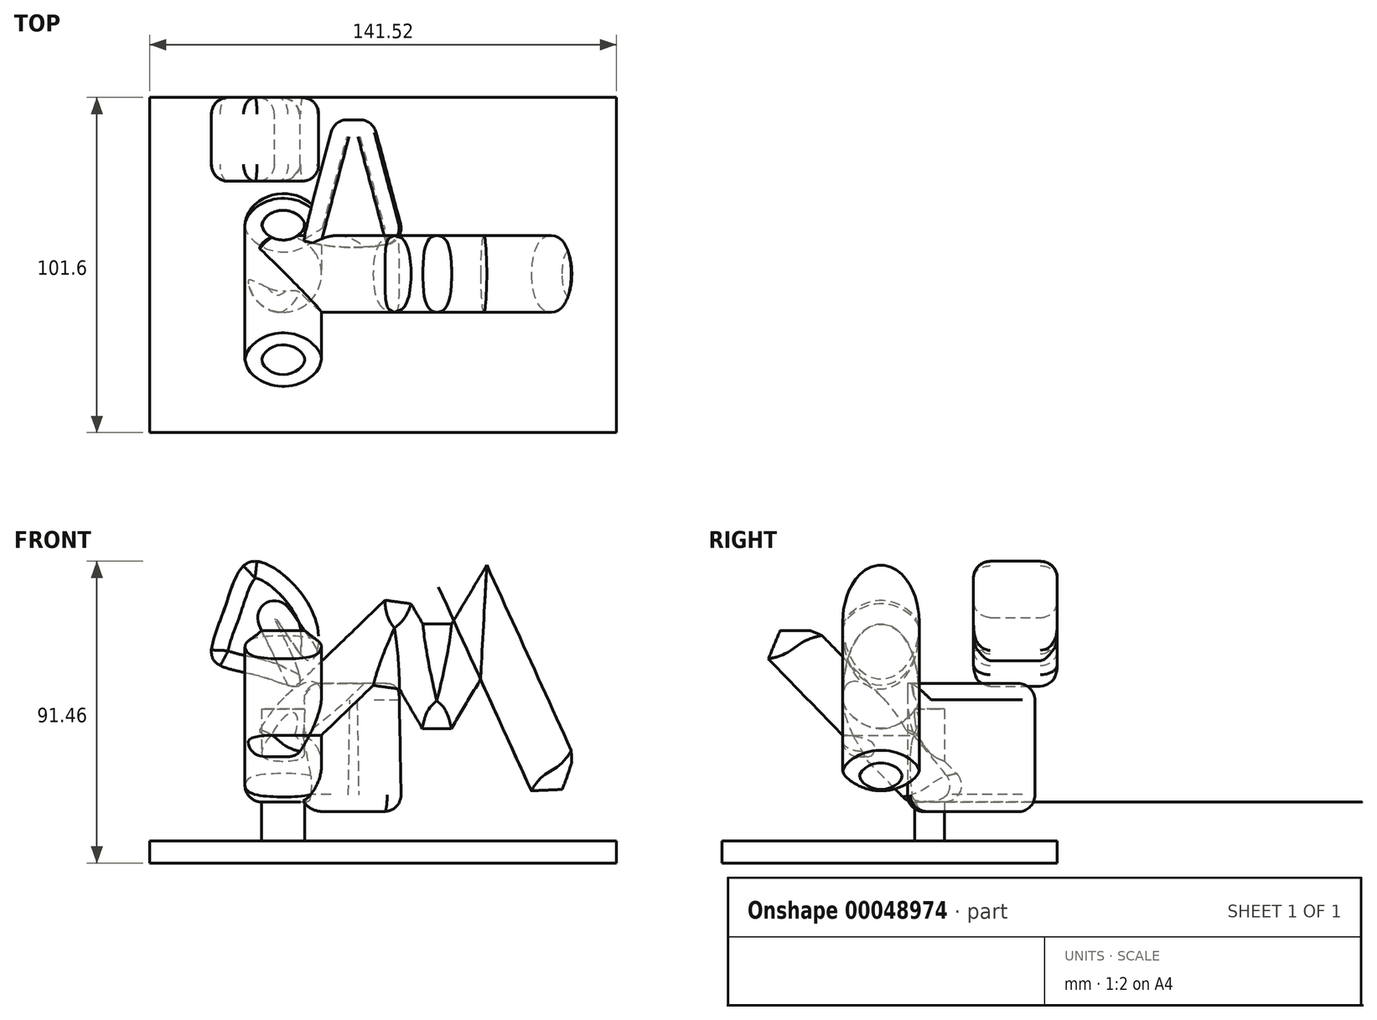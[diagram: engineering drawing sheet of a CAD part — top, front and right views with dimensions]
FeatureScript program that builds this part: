
annotation { "Feature Type Name" : "Feature", "Feature Type Description" : "" }
export const myFeature = defineFeature(function(context is Context, id is Id, definition is map)
    precondition{}
    {
        {
            var Q0;
            Q0=qCreatedBy(makeId("Front.planeOp"),FACE);
            var sketch = newSketch(context, id + "F0", { "sketchPlane" : qUnion([Q0])});
            skFitSpline(sketch, "E0", {"points": [v(-11.66, 35.52) * mm, v(-30.7, 52.67) * mm, v(-39.27, 37.93) * mm, v(-42.48, 22.92) * mm, v(-27.2, 17.56) * mm, v(-16.22, 15.95) * mm, v(-23.99, 35.52) * mm, v(-19.97, 30.15) * mm, v(-13, 22.65) * mm, v(-11.66, 35.52) * mm]});
            skSolve(sketch);
        }
        {
            var Q0;
            Q0=makeQuery(id+"F0.imprint","IMPRINT",FACE,{"disambiguationData":[TD([[makeQuery(id+"F0.imprint","IMPRINT",EDGE,{"derivedFrom":sQuery(id+"F0.wireOp",EDGE,"E0")}),1.0]])]});
            extrude(context, id + "F1", {"entities" : qUnion([Q0]), "depth" : 25.4 * mm});
        }
        {
            var Q0;
            Q0=qCreatedBy(makeId("Right.planeOp"),FACE);
            var sketch = newSketch(context, id + "F2", { "sketchPlane" : qUnion([Q0])});
            skLineSegment(sketch, "E1.bottom", {"start": v(-45.43, 15.68) * mm, "end": v(-6.84, 15.68) * mm});
            skLineSegment(sketch, "E1.top", {"start": v(-45.43, -23.19) * mm, "end": v(-6.84, -23.19) * mm});
            skLineSegment(sketch, "E1.left", {"start": v(-45.43, 15.68) * mm, "end": v(-45.43, -23.19) * mm});
            skLineSegment(sketch, "E1.right", {"start": v(-6.84, 15.68) * mm, "end": v(-6.84, -23.19) * mm});
            skLineSegment(sketch, "E2", {"start": v(-53.47, -19.97) * mm, "end": v(-12.2, 31.76) * mm});
            skLineSegment(sketch, "E3", {"start": v(-12.2, 31.76) * mm, "end": v(38.46, -20.24) * mm});
            skLineSegment(sketch, "E4", {"start": v(16.75, -41.5) * mm, "end": v(10.86, 39.23) * mm});
            skSolve(sketch);
        }
        {
            var Q0;
            Q0=qCreatedBy(makeId("Top.planeOp"),FACE);
            var sketch = newSketch(context, id + "F3", { "sketchPlane" : qUnion([Q0])});
            skCircle(sketch, "E5", {"center": v(-21.3, -53.47) * mm, "radius": 11.6 * mm});
            skSolve(sketch);
        }
        {
            var Q0;
            Q0 = qSketchRegion(id + "F2", true);
            var Q1;
            Q1=sQuery(id+"F2.wireOp",EDGE,"E4");
            revolve(context, id + "F4", {"entities" : qUnion([Q0]), "axis" : qUnion([Q1]), "revolveType" : RevolveType.SYMMETRIC, "angle" : 30 * degree});
        }
        {
            var Q0;
            Q0=qCreatedBy(makeId("Front.planeOp"),FACE);
            var sketch = newSketch(context, id + "F5", { "sketchPlane" : qUnion([Q0])});
            skLineSegment(sketch, "E6", {"start": v(-39, -6.57) * mm, "end": v(14.07, 44.63) * mm});
            skLineSegment(sketch, "E7", {"start": v(14.07, 44.63) * mm, "end": v(25.33, 25.33) * mm});
            skLineSegment(sketch, "E8", {"start": v(25.33, 25.33) * mm, "end": v(40.34, 50.53) * mm});
            skLineSegment(sketch, "E9", {"start": v(40.34, 50.53) * mm, "end": v(66.6, -7.1) * mm});
            skSolve(sketch);
        }
        {
            var Q0;
            Q0=makeQuery(id+"F3.imprint","IMPRINT",FACE,{"disambiguationData":[TD([[makeQuery(id+"F3.imprint","IMPRINT",EDGE,{"derivedFrom":sQuery(id+"F3.wireOp",EDGE,"E5")}),1.0]])]});
            var Q1;
            Q1=sQuery(id+"F5.wireOp",EDGE,"E6");
            var Q2;
            Q2=sQuery(id+"F5.wireOp",EDGE,"E7");
            var Q3;
            Q3=sQuery(id+"F5.wireOp",EDGE,"E8");
            var Q4;
            Q4=sQuery(id+"F5.wireOp",EDGE,"E9");
            sweep(context, id + "F6", {"operationType" : NewBodyOperationType.ADD, "profiles" : qUnion([Q0]), "path" : qUnion([Q1, Q2, Q3, Q4])});
        }
        {
            var Q0;
            Q0 = qSketchRegion(id + "F3", true);
            var Q1;
            Q1=sQuery(id+"F2.wireOp",EDGE,"E3");
            sweep(context, id + "F7", {"profiles" : qUnion([Q0]), "path" : qUnion([Q1])});
        }
        {
            var Q0;
            Q0=makeQuery(id+"F6.opSweep","CAP_EDGE",EDGE,{"disambiguationData":[OSD([sQuery(id+"F3.wireOp",EDGE,"E5"),sQuery(id+"F5.wireOp",VERTEX,"E6.start")])],"isStart":true});
            fillet(context, id + "F8", {"entities" : qUnion([Q0]), "radius" : 5.08 * mm, "tangentPropagation" : true, "allowEdgeOverflow" : false});
        }
        {
            var Q0;
            Q0=makeQuery(id+"F7.opSweep","CAP_EDGE",EDGE,{"disambiguationData":[OSD([sQuery(id+"F2.wireOp",VERTEX,"E3.end"),sQuery(id+"F3.wireOp",EDGE,"E5")])],"isStart":true});
            fillet(context, id + "F9", {"entities" : qUnion([Q0]), "radius" : 5.08 * mm, "tangentPropagation" : true, "allowEdgeOverflow" : false});
        }
        {
            var Q0;
            Q0=makeQuery(id+"F4.opRevolve","CAP_EDGE",EDGE,{"disambiguationData":[OSD([sQuery(id+"F2.wireOp",EDGE,"E1.left")])],"isStart":false});
            var Q1;
            Q1=makeQuery(id+"F4.opRevolve","SWEPT_EDGE",EDGE,{"disambiguationData":[OSD([sQuery(id+"F2.wireOp",EDGE,"E1.top"),sQuery(id+"F2.wireOp",EDGE,"E1.left")])]});
            var Q2;
            Q2=makeQuery(id+"F4.opRevolve","CAP_EDGE",EDGE,{"disambiguationData":[OSD([sQuery(id+"F2.wireOp",EDGE,"E1.top")])],"isStart":true});
            var Q3;
            Q3=makeQuery(id+"F4.opRevolve","CAP_EDGE",EDGE,{"disambiguationData":[OSD([sQuery(id+"F2.wireOp",EDGE,"E1.top")])],"isStart":false});
            var Q4;
            Q4=makeQuery(id+"F4.opRevolve","SWEPT_EDGE",EDGE,{"disambiguationData":[OSD([sQuery(id+"F2.wireOp",EDGE,"E1.top"),sQuery(id+"F2.wireOp",EDGE,"E1.right")])]});
            var Q5;
            Q5=makeQuery(id+"F4.opRevolve","CAP_EDGE",EDGE,{"disambiguationData":[OSD([sQuery(id+"F2.wireOp",EDGE,"E1.right")])],"isStart":false});
            var Q6;
            Q6=makeQuery(id+"F4.opRevolve","CAP_EDGE",EDGE,{"disambiguationData":[OSD([sQuery(id+"F2.wireOp",EDGE,"E1.right")])],"isStart":true});
            var Q7;
            Q7=makeQuery(id+"F4.opRevolve","CAP_EDGE",EDGE,{"disambiguationData":[OSD([sQuery(id+"F2.wireOp",EDGE,"E1.bottom")])],"isStart":false});
            var Q8;
            Q8=makeQuery(id+"F4.opRevolve","CAP_EDGE",EDGE,{"disambiguationData":[OSD([sQuery(id+"F2.wireOp",EDGE,"E1.bottom")])],"isStart":true});
            var Q9;
            Q9=makeQuery(id+"F4.opRevolve","SWEPT_EDGE",EDGE,{"disambiguationData":[OSD([sQuery(id+"F2.wireOp",EDGE,"E1.bottom"),sQuery(id+"F2.wireOp",EDGE,"E1.right")])]});
            fillet(context, id + "F10", {"entities" : qUnion([Q0, Q1, Q2, Q3, Q4, Q5, Q6, Q7, Q8, Q9]), "radius" : 5.08 * mm, "tangentPropagation" : true, "allowEdgeOverflow" : false});
        }
        {
            var Q0;
            Q0=makeQuery(id+"F6.opSweep","MID_CAP_EDGE",EDGE,{"disambiguationData":[OSD([sQuery(id+"F3.wireOp",EDGE,"E5"),sQuery(id+"F5.wireOp",VERTEX,"E8.start")])],"capPos":2.0});
            var Q1;
            Q1=makeQuery(id+"F6.opSweep","CAP_EDGE",EDGE,{"disambiguationData":[OSD([sQuery(id+"F3.wireOp",EDGE,"E5"),sQuery(id+"F5.wireOp",VERTEX,"E9.end")])],"isStart":false});
            var Q2;
            Q2=makeQuery(id+"F6.opSweep","MID_CAP_EDGE",EDGE,{"disambiguationData":[OSD([sQuery(id+"F3.wireOp",EDGE,"E5"),sQuery(id+"F5.wireOp",VERTEX,"E7.start")])],"capPos":1.0});
            var Q3;
            Q3=makeQuery(id+"F7.opSweep","CAP_EDGE",EDGE,{"disambiguationData":[OSD([sQuery(id+"F2.wireOp",VERTEX,"E3.start"),sQuery(id+"F3.wireOp",EDGE,"E5")])],"isStart":false});
            chamfer(context, id + "F11", {"entities" : qUnion([Q0, Q1, Q2, Q3]), "width" : 5.08 * mm, "tangentPropagation" : true});
        }
        {
            var Q0;
            Q0=makeQuery(id+"F1.opExtrude","CAP_EDGE",EDGE,{"disambiguationData":[OSD([sQuery(id+"F0.wireOp",EDGE,"E0")])],"isStart":false});
            var Q1;
            Q1=makeQuery(id+"F1.opExtrude","CAP_EDGE",EDGE,{"disambiguationData":[OSD([sQuery(id+"F0.wireOp",EDGE,"E0")])],"isStart":true});
            fillet(context, id + "F12", {"entities" : qUnion([Q0, Q1]), "radius" : 5.08 * mm, "tangentPropagation" : true, "allowEdgeOverflow" : false});
        }
        {
            var Q0;
            Q0=qCreatedBy(makeId("Front.planeOp"),FACE);
            var sketch = newSketch(context, id + "F13", { "sketchPlane" : qUnion([Q0])});
            skLineSegment(sketch, "E10.bottom", {"start": v(-61.78, -32.03) * mm, "end": v(79.74, -32.03) * mm});
            skLineSegment(sketch, "E10.top", {"start": v(-61.78, -38.73) * mm, "end": v(79.74, -38.73) * mm});
            skLineSegment(sketch, "E10.left", {"start": v(-61.78, -32.03) * mm, "end": v(-61.78, -38.73) * mm});
            skLineSegment(sketch, "E10.right", {"start": v(79.74, -32.03) * mm, "end": v(79.74, -38.73) * mm});
            skLineSegment(sketch, "E11", {"start": v(-21.68, 7.9) * mm, "end": v(-21.68, -32.03) * mm});
            skLineSegment(sketch, "E12", {"start": v(0, -23.19) * mm, "end": v(0, -32.03) * mm});
            skLineSegment(sketch, "E13", {"start": v(50.96, -32.03) * mm, "end": v(50.96, -8.44) * mm});
            skSolve(sketch);
        }
        {
            var Q0;
            Q0=makeQuery(id+"F13.imprint","IMPRINT",FACE,{"disambiguationData":[TD([[makeQuery(id+"F13.imprint","IMPRINT",EDGE,{"derivedFrom":sQuery(id+"F13.wireOp",EDGE,"E10.bottom")}),-1.0]])]});
            extrude(context, id + "F14", {"entities" : qUnion([Q0]), "depth" : 101.6 * mm});
        }
        {
            var Q0;
            Q0 = qSketchRegion(id + "F13", true);
            extrude(context, id + "F15", {"entities" : qUnion([Q0]), "operationType" : NewBodyOperationType.ADD, "depth" : 25.4 * mm});
        }
        {
            var Q0;
            Q0=makeQuery(id+"F7.opSweep","CAP_FACE",FACE,{"disambiguationData":[OSD([sQuery(id+"F2.wireOp",VERTEX,"E3.end"),sQuery(id+"F3.wireOp",EDGE,"E5")])],"isStart":true});
            var Q1;
            {var subQ0=sQuery(id+"F3.wireOp",EDGE,"E5");var subQ1=sQuery(id+"F2.wireOp",VERTEX,"E3.end");Q1=makeQuery(id+"F9.opFillet","BLEND_EDGE",EDGE,{"blendedFrom":[makeQuery(id+"F7.opSweep","CAP_EDGE",EDGE,{"disambiguationData":[OSD([subQ1,subQ0])],"isStart":true}),makeQuery(id+"F7.opSweep","CAP_FACE",FACE,{"disambiguationData":[OSD([subQ1,subQ0])],"isStart":true})],"blendedInto":[makeQuery(id+"F7.opSweep","CAP_FACE",FACE,{"disambiguationData":[OSD([subQ1,subQ0])],"isStart":true})]});}
            var Q2;
            Q2=sQuery(id+"F13.wireOp",EDGE,"E11");
            sweep(context, id + "F16", {"operationType" : NewBodyOperationType.ADD, "profiles" : qUnion([Q0]), "surfaceProfiles" : qUnion([Q1]), "path" : qUnion([Q2])});
        }
    });
